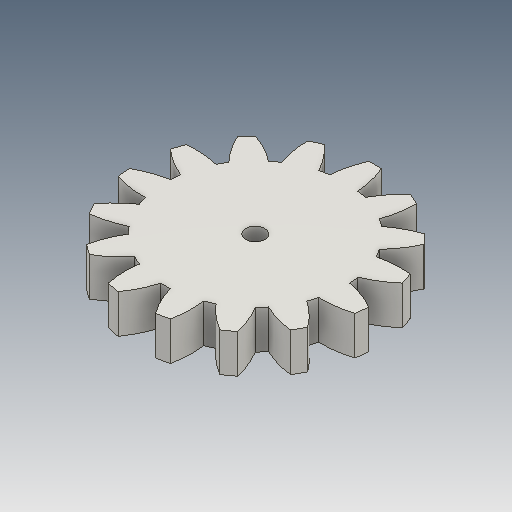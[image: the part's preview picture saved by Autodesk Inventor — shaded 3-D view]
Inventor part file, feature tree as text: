
AUTODESK INVENTOR PART (.ipt)
format: ipt  version: 2018 (Build 220112000, 112)  size: 226,816 bytes
history: native  units: mm
features: other x13, sketch x4, plane x4
ambient origin geometry x8: Origin, YZ Plane, XZ Plane, XY Plane, X Axis, Y Axis, Z Axis, Center Point
bodies: Volumenkörper1 (feature_tree)
feature tree (21):
  other  "Stirnzahnrad21_MIR.ipt"
  other  "Volumenkörper1::Stirnzahnrad21_MIR.ipt"
  other  "Bezeichnung1"
  sketch  "Sketch1"  dims[d0=10.0mm]
  sketch  "Sketch2"  dims[d16=40.0mm d17=0.0mm d41=0.0mm d43=40.0mm d46=40.0mm d47=0.0mm d48=0.0mm]
  sketch  "Skizze3"
  sketch  "Skizze4"
  plane  "XZ Plane_1"
  plane  "Work Plane2"
  plane  "Work Plane8"
  plane  "Work Plane9"
  other  "Z Axis_1"
  other  "Flä1"
  other  "Flä1::Abgeleitet"
  other  "Abstands-iMate"
  other  "Ausrichtungs-iMate"
  other  "Netz-iMate"
  other  "Achsen-iMate"
  other  "Positions-iMate"
  other  "Netz-iMate 2"
  other  "Startebenen-iMate"
